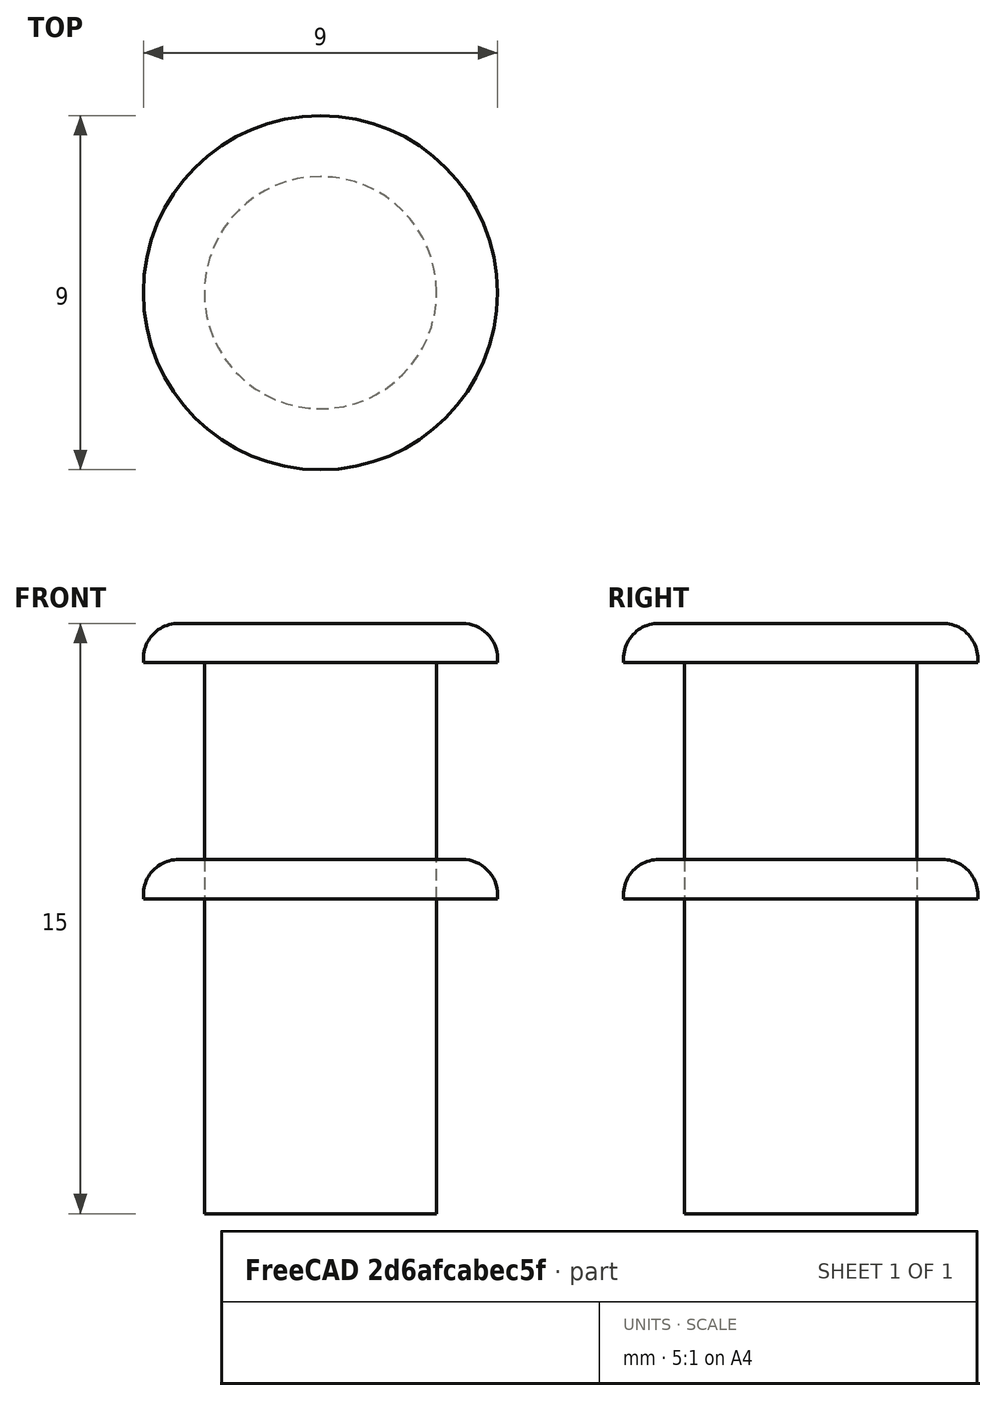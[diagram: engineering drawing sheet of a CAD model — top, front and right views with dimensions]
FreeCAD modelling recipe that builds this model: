
FCSTD DOCUMENT  (FreeCAD 1.0R39109 (Git))
Label: tapon
License: All rights reserved
LicenseURL: http://en.wikipedia.org/wiki/All_rights_reserved
objects: Part::Cylinder×4, Part::Fillet×2, Part::Fuse×2, Mesh::Feature×2
note: 8 computed .brp shape members not serialized (recipe doc carries the construction recipe); baked Part::Feature solids carry a one-line shape summary decoded from their .brp

FEATURE [Part::Cylinder] Cylinder
  Angle = 360
  AttacherType = Attacher::AttachEngine3D
  FirstAngle = 0
  Height = 15
  Radius = 2.95
  SecondAngle = 0
FEATURE [Part::Cylinder] Cylinder001
  Angle = 360
  AttacherType = Attacher::AttachEngine3D
  FirstAngle = 0
  Height = 1
  Placement = pos=(0,0,14) rot=(0,0,1;0rad)
  Radius = 4.5
  SecondAngle = 0
FEATURE [Part::Fillet] Fillet
  Base = -> Cylinder001
  EdgeLinks = -> Cylinder001 [Edge3]
  Edges = 1 edges r=0.9: [Edge3]
FEATURE [Part::Fuse] Fusion
  Base = -> Cylinder
  Tool = -> Fillet
FEATURE [Part::Cylinder] Cylinder002
  Angle = 360
  AttacherType = Attacher::AttachEngine3D
  FirstAngle = 0
  Height = 8
  Radius = 2.95
  SecondAngle = 0
FEATURE [Part::Cylinder] Cylinder003
  Angle = 360
  AttacherType = Attacher::AttachEngine3D
  FirstAngle = 0
  Height = 1
  Placement = pos=(0,0,8) rot=(0,0,1;0rad)
  Radius = 4.5
  SecondAngle = 0
FEATURE [Part::Fillet] Fillet001
  Base = -> Cylinder003
  EdgeLinks = -> Cylinder003 [Edge3]
  Edges = 1 edges r=0.9: [Edge3]
FEATURE [Part::Fuse] Fusion001
  Base = -> Cylinder002
  Tool = -> Fillet001
FEATURE [Mesh::Feature] Mesh  label="Fusion (Meshed)"
FEATURE [Mesh::Feature] Mesh001  label="Fusion001 (Meshed)"
